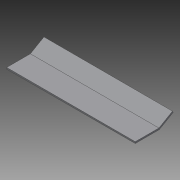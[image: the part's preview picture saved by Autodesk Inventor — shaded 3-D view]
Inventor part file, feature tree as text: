
AUTODESK INVENTOR PART (.ipt)
format: ipt  version: 2015 (Build 190159000, 159)  size: 80,384 bytes
history: native  units: mm
features: extrude x2, sketch x2
ambient origin geometry x8: Origin, YZ Plane, XZ Plane, XY Plane, X Axis, Y Axis, Z Axis, Center Point
bodies: Body1 (feature_tree)
feature tree (4):
  extrude  "押し出し2"  Depth=80.0mm
  extrude  "押し出し3"  Depth=15.0mm
  sketch  "スケッチ2"
  sketch  "スケッチ3"
